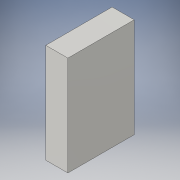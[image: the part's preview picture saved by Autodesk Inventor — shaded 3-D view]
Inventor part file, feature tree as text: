
AUTODESK INVENTOR PART (.ipt)
format: ipt  version: 2016 (Build 200138000, 138)  size: 85,504 bytes
history: native  units: in
note: dims shown in document units (in); Inventor stores cm internally (conversion verified against a paired STEP export)
features: extrude x1, sketch x1
ambient origin geometry x8: Origin, YZ Plane, XZ Plane, XY Plane, X Axis, Y Axis, Z Axis, Center Point
bodies: Solid1 (feature_tree)
feature tree (2):
  extrude  "Extrusion1"  Depth=12.0in
  sketch  "Sketch1"  dims[d0=18.0in d1=12.0in d2=4.0in d3=0.0in]
